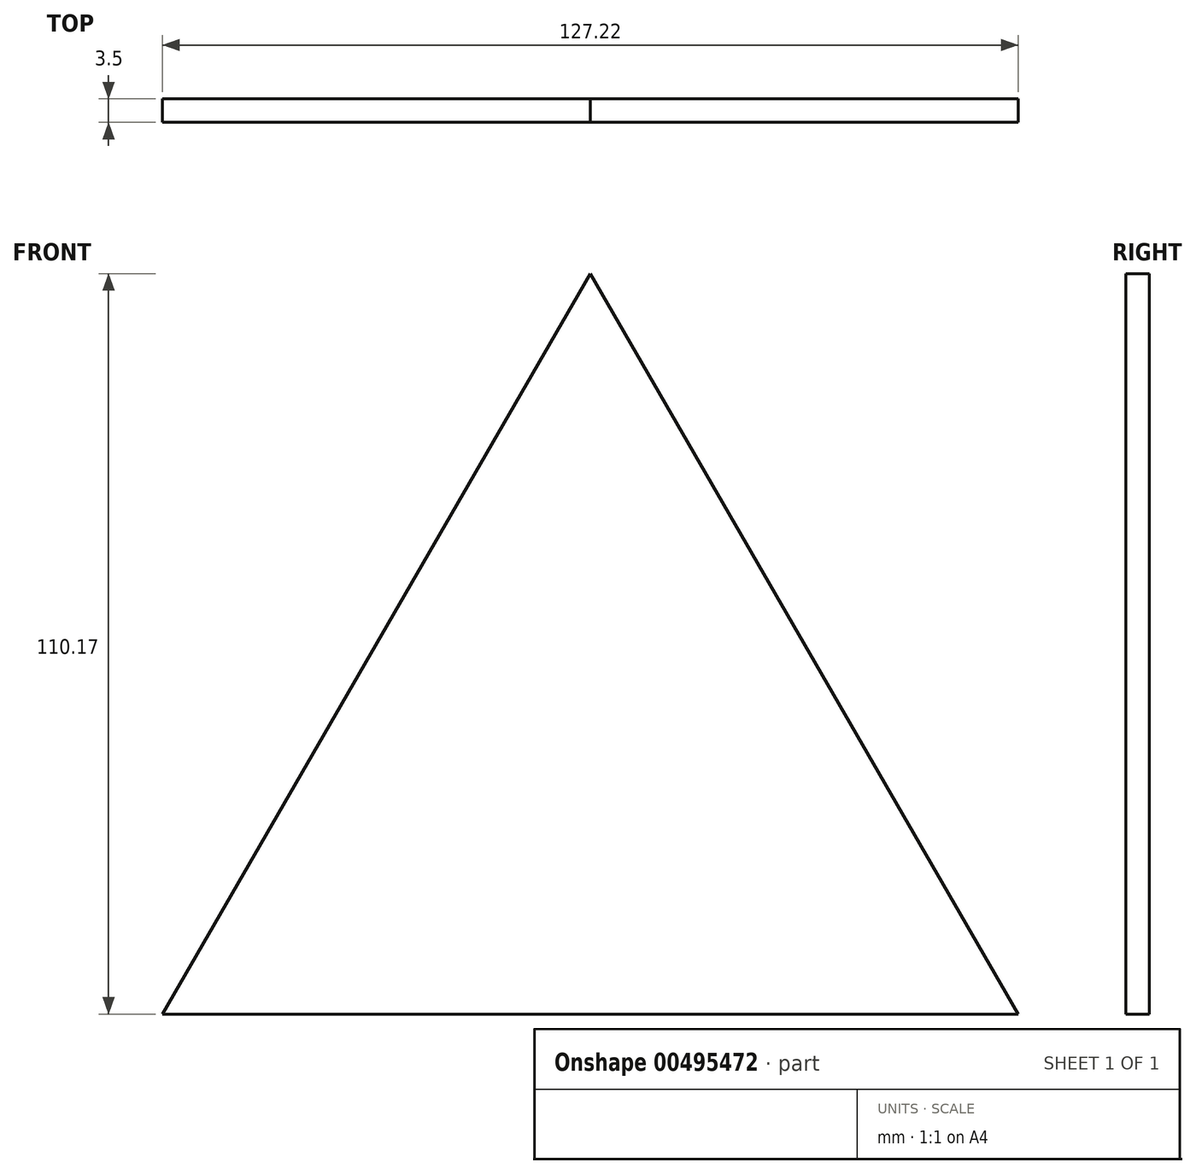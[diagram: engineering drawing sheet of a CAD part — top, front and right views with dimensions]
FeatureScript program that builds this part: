
annotation { "Feature Type Name" : "Feature", "Feature Type Description" : "" }
export const myFeature = defineFeature(function(context is Context, id is Id, definition is map)
    precondition{}
    {
        {
            var Q0;
            Q0=qCreatedBy(makeId("Front.planeOp"),FACE);
            var sketch = newSketch(context, id + "F0", { "sketchPlane" : qUnion([Q0])});
            skLineSegment(sketch, "E0.0", {"start": v(0, 73.45) * mm, "end": v(63.6, -36.72) * mm});
            skLineSegment(sketch, "E0.1", {"start": v(63.6, -36.72) * mm, "end": v(-63.6, -36.72) * mm});
            skLineSegment(sketch, "E0.2", {"start": v(-63.6, -36.72) * mm, "end": v(0, 73.45) * mm});
            skPoint(sketch, "E0.0.midPoint", {"position": v(31.8, 18.36) * mm});
            skSolve(sketch);
        }
        {
            var Q0;
            Q0=makeQuery(id+"F0.imprint","IMPRINT",FACE,{"disambiguationData":[TD([[makeQuery(id+"F0.imprint","IMPRINT",EDGE,{"derivedFrom":sQuery(id+"F0.wireOp",EDGE,"E0.0")}),-1.0]])]});
            extrude(context, id + "F1", {"entities" : qUnion([Q0]), "depth" : 3.5 * mm});
        }
    });
